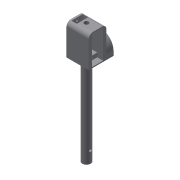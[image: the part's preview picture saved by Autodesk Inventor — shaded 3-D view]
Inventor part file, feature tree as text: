
AUTODESK INVENTOR PART (.ipt)
format: ipt  version: 2018 (Build 220112000, 112)  size: 269,312 bytes
history: native  units: mm
features: sketch x13, extrude x12, fillet x3, other x1
ambient origin geometry x8: Origin, YZ Plane, XZ Plane, XY Plane, X Axis, Y Axis, Z Axis, Center Point
bodies: Solid1 (feature_tree)
feature tree (29):
  extrude  "base"  Depth=20.0mm
  extrude  "attacher"  Depth=10.0mm
  fillet  "Fillet2"  Radius=9.5mm
  extrude  "hole_bar_rigify"  Depth=4.0mm
  extrude  "servo_place"  Depth=12.0mm TaperAngle=0.0deg
  extrude  "servo_place_2"  Depth=11.6mm
  extrude  "screw_holes"  Depth=23.2mm
  fillet  "Fillet3"  Radius=23.0mm
  extrude  "rot_axis"  Depth=4.7mm
  extrude  "cable_hole"  Depth=1.9mm
  fillet  "Fillet5"  Radius=1.9mm
  extrude  "cable_guide_1"  Depth=2.0mm
  sketch  "Sketch23"  dims[d90=6.6mm d91=0.0mm d92=20.0mm]
  sketch  "Sketch24"  dims[d93=5.0mm d94=11.0mm]
  extrude  "cable_guide_2"  Depth=20.0mm
  extrude  "cable_guide_3"  Depth=11.0mm
  other  "cable_guide_4"
  extrude  "Extrusion25"  Depth=10.0mm TaperAngle=0.0deg
  sketch  "Sketch1"  dims[d0=25.0mm d1=20.0mm]
  sketch  "Sketch4"  dims[d2=35.0mm d3=0.0mm d18=10.0mm d19=9.5mm]
  sketch  "Sketch5"  dims[d20=100.0mm d21=0.0mm d22=4.0mm]
  sketch  "Sketch15"  dims[d23=5.0mm d24=12.0mm d25=0.0mm]
  sketch  "Sketch16"  dims[d76=6.25mm d77=11.6mm]
  sketch  "Sketch17"  dims[d78=12.5mm d79=23.2mm d80=23.0mm d81=0.0mm]
  sketch  "Sketch18"  dims[d82=4.7mm d83=4.7mm]
  sketch  "Sketch21"  dims[d84=6.6mm d85=0.0mm d86=1.9mm d87=1.9mm]
  sketch  "Sketch22"  dims[d88=2.0mm d89=2.0mm]
  sketch  "Sketch25"  dims[d95=10.0mm d96=8.0mm d97=0.0mm]
  sketch  "Sketch26"  dims[d105=6.0mm d106=10.0mm d107=0.0mm d108=6.0mm d109=10.0mm d110=5.0mm d111=5.0mm d112=5.0mm d113=5.0mm d114=15.0mm d115=15.0mm d116=5.0mm d117=15.0mm d118=8.0mm d119=0.0mm d120=2.0mm d121=11.0mm d122=7.0mm d123=2.0mm d124=11.0mm d125=7.0mm d126=8.0mm d127=0.0mm d128=8.0mm d129=0.0mm d130=90.0deg d131=13.0mm d132=3.0mm d133=10.0mm d134=0.0mm]
